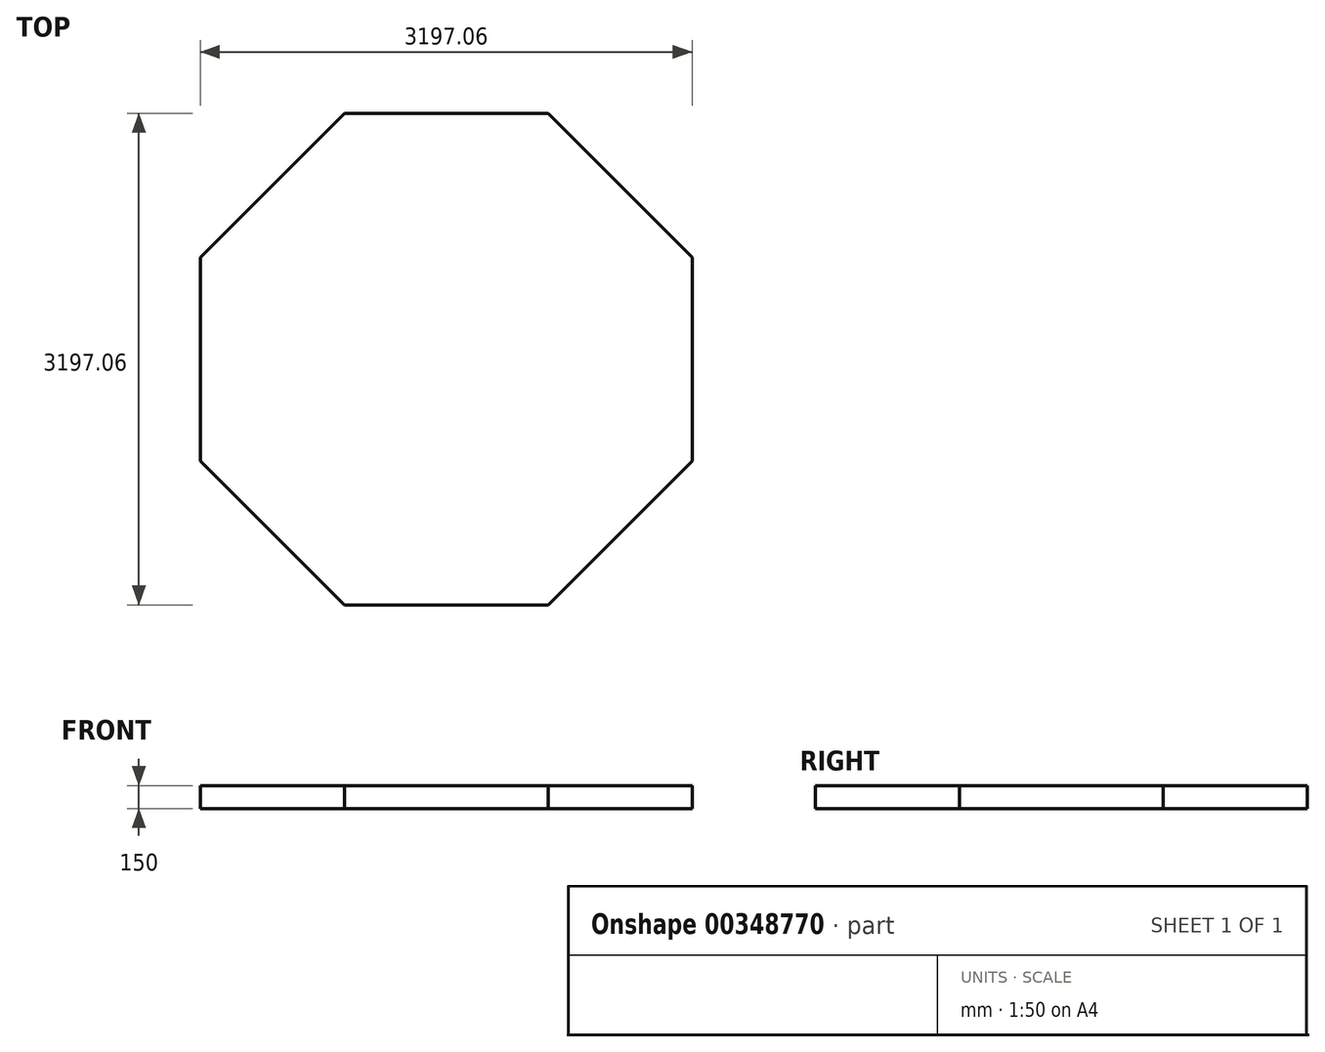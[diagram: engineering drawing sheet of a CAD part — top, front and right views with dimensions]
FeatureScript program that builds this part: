
annotation { "Feature Type Name" : "Feature", "Feature Type Description" : "" }
export const myFeature = defineFeature(function(context is Context, id is Id, definition is map)
    precondition{}
    {
        {
            var Q0;
            Q0=qCreatedBy(makeId("Top.planeOp"),FACE);
            var sketch = newSketch(context, id + "F0", { "sketchPlane" : qUnion([Q0])});
            skCircle(sketch, "E0.cCircle", {"center": v(-1367.36, 467.23) * mm, "radius": 1448.53 * mm, "construction": true});
            skLineSegment(sketch, "E0.0", {"start": v(81.17, -132.77) * mm, "end": v(-767.36, -981.3) * mm});
            skLineSegment(sketch, "E0.1", {"start": v(-767.36, -981.3) * mm, "end": v(-1967.36, -981.3) * mm});
            skLineSegment(sketch, "E0.2", {"start": v(-1967.36, -981.3) * mm, "end": v(-2815.9, -132.77) * mm});
            skLineSegment(sketch, "E0.3", {"start": v(-2815.9, -132.77) * mm, "end": v(-2815.9, 1067.23) * mm});
            skLineSegment(sketch, "E0.4", {"start": v(-2815.9, 1067.23) * mm, "end": v(-1967.36, 1915.76) * mm});
            skLineSegment(sketch, "E0.5", {"start": v(-1967.36, 1915.76) * mm, "end": v(-767.36, 1915.76) * mm});
            skLineSegment(sketch, "E0.6", {"start": v(-767.36, 1915.76) * mm, "end": v(81.17, 1067.23) * mm});
            skLineSegment(sketch, "E0.7", {"start": v(81.17, 1067.23) * mm, "end": v(81.17, -132.77) * mm});
            skPoint(sketch, "E0.0.midPoint", {"position": v(-343.1, -557.03) * mm});
            skLineSegment(sketch, "E1.0", {"start": v(-2965.9, -194.9) * mm, "end": v(-2965.9, 1129.37) * mm});
            skLineSegment(sketch, "E1.1", {"start": v(-2029.5, -1131.3) * mm, "end": v(-2965.9, -194.9) * mm});
            skLineSegment(sketch, "E1.2", {"start": v(-2965.9, 1129.37) * mm, "end": v(-2029.5, 2065.76) * mm});
            skLineSegment(sketch, "E1.3", {"start": v(-705.23, -1131.3) * mm, "end": v(-2029.5, -1131.3) * mm});
            skLineSegment(sketch, "E1.4", {"start": v(-2029.5, 2065.76) * mm, "end": v(-705.23, 2065.76) * mm});
            skLineSegment(sketch, "E1.5", {"start": v(-705.23, 2065.76) * mm, "end": v(231.17, 1129.37) * mm});
            skLineSegment(sketch, "E1.6", {"start": v(231.17, 1129.37) * mm, "end": v(231.17, -194.9) * mm});
            skLineSegment(sketch, "E1.7", {"start": v(231.17, -194.9) * mm, "end": v(-705.23, -1131.3) * mm});
            skLineSegment(sketch, "E2", {"start": v(-2965.9, 467.23) * mm, "end": v(231.17, 467.23) * mm, "construction": true});
            skSolve(sketch);
        }
        {
            var Q0;
            Q0=makeQuery(id+"F0.imprint","IMPRINT",FACE,{"disambiguationData":[TD([[makeQuery(id+"F0.imprint","IMPRINT",EDGE,{"derivedFrom":sQuery(id+"F0.wireOp",EDGE,"E0.0")}),1.0]])]});
            var Q1;
            Q1=makeQuery(id+"F0.imprint","IMPRINT",FACE,{"disambiguationData":[TD([[makeQuery(id+"F0.imprint","IMPRINT",EDGE,{"derivedFrom":sQuery(id+"F0.wireOp",EDGE,"E0.0")}),-1.0]])]});
            extrude(context, id + "F1", {"entities" : qUnion([Q0, Q1]), "depth" : 150 * mm});
        }
    });
